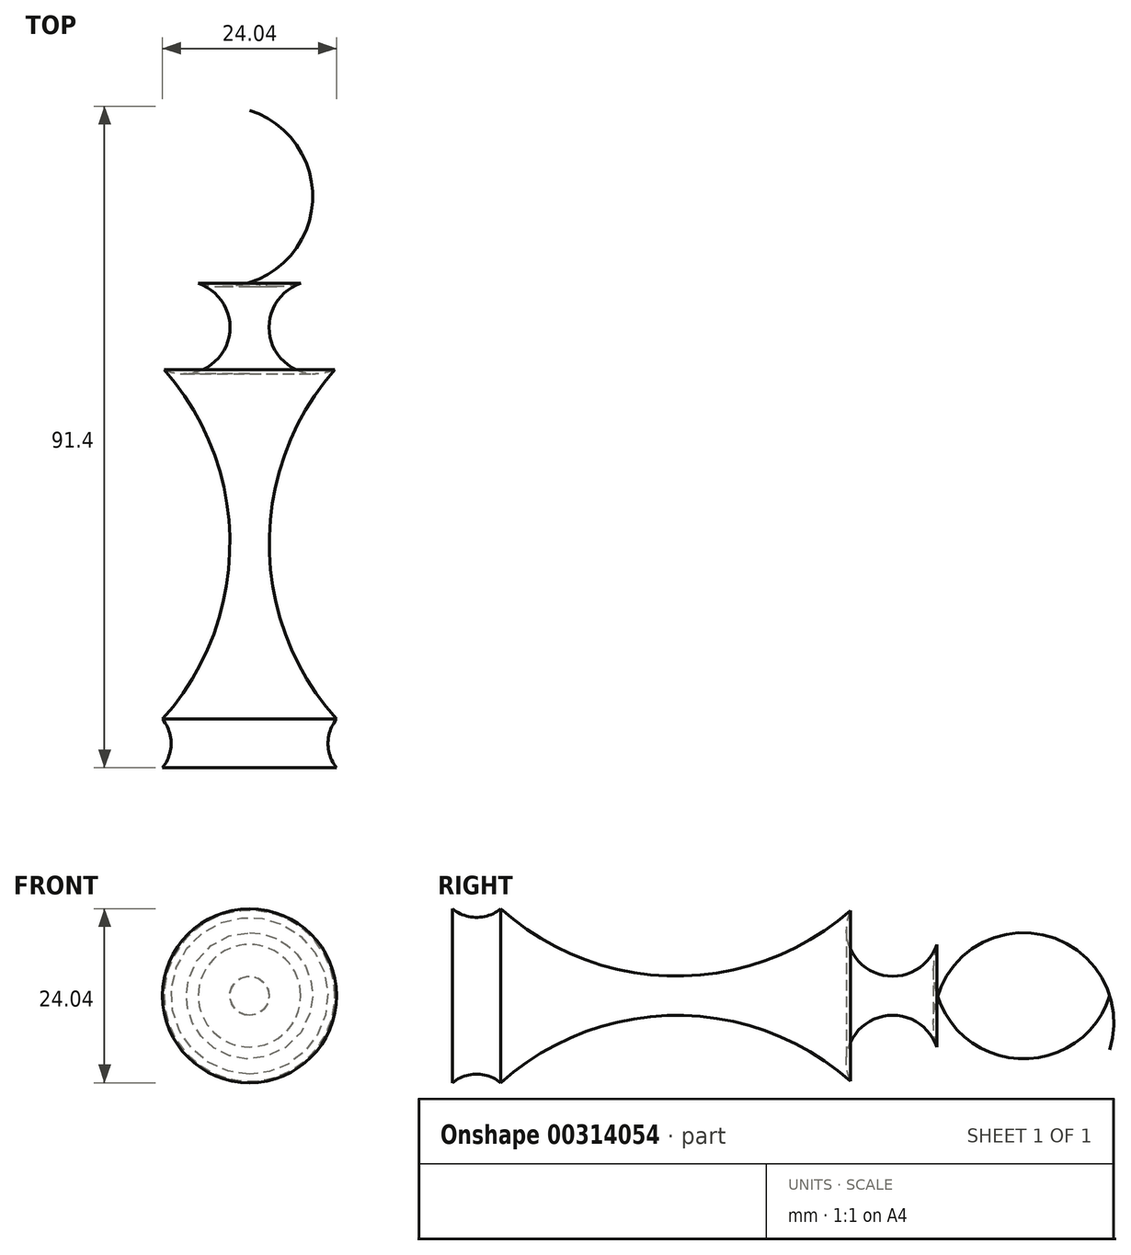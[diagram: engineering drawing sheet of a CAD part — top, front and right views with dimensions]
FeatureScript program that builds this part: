
annotation { "Feature Type Name" : "Feature", "Feature Type Description" : "" }
export const myFeature = defineFeature(function(context is Context, id is Id, definition is map)
    precondition{}
    {
        {
            var Q0;
            Q0=qCreatedBy(makeId("Top.planeOp"),FACE);
            var sketch = newSketch(context, id + "F0", { "sketchPlane" : qUnion([Q0])});
            skLineSegment(sketch, "E0", {"start": v(0, 46.48) * mm, "end": v(0, -44.34) * mm});
            skLineSegment(sketch, "E1", {"start": v(0, -44.34) * mm, "end": v(0, 46.48) * mm});
            skArc(sketch, "E2", {"start": v(0, 22.7) * mm, "mid": v(16.22, 34.59) * mm, "end": v(0, 46.48) * mm});
            skArc(sketch, "E3", {"start": v(7.5, 22.7) * mm, "mid": v(3.06, 14.34) * mm, "end": v(11.78, 10.66) * mm});
            skArc(sketch, "E4", {"start": v(11.78, 10.66) * mm, "mid": v(2.72, -13.54) * mm, "end": v(12.02, -37.64) * mm});
            skLineSegment(sketch, "E5", {"start": v(0, -44.34) * mm, "end": v(12.02, -44.34) * mm});
            skLineSegment(sketch, "E6", {"start": v(12.02, -44.34) * mm, "end": v(1.38, -44.34) * mm});
            skLineSegment(sketch, "E7", {"start": v(1.38, -44.34) * mm, "end": v(12.02, -44.34) * mm});
            skArc(sketch, "E8", {"start": v(12.02, -37.64) * mm, "mid": v(10.84, -41) * mm, "end": v(12.02, -44.34) * mm});
            skSolve(sketch);
        }
        {
            var Q0;
            {var subQ0=sQuery(id+"F0.wireOp",EDGE,"E4");Q0=makeQuery(id+"F0.imprint","IMPRINT",FACE,{"disambiguationData":[TD([[makeQuery(id+"F0.imprint","IMPRINT",EDGE,{"derivedFrom":subQ0}),-1.0]])]});}
            var Q1;
            {var subQ0=sQuery(id+"F0.wireOp",EDGE,"E2");var subQ1=sQuery(id+"F0.wireOp",EDGE,"E1");var subQ2=makeQuery(id+"F0.imprint","INTERSECT",VERTEX,{"disambiguationData":[OD(0.0)],"derivedFrom":[subQ1,subQ0]});Q1=makeQuery(id+"F0.imprint","IMPRINT",FACE,{"disambiguationData":[TD([[makeQuery(id+"F0.imprint","IMPRINT",EDGE,{"disambiguationData":[TD([[subQ2,1.0]])],"derivedFrom":subQ1}),-1.0]])]});}
            var Q2;
            Q2=sQuery(id+"F0.wireOp",EDGE,"E1");
            revolve(context, id + "F1", {"entities" : qUnion([Q0, Q1]), "axis" : qUnion([Q2]), "revolveType" : RevolveType.FULL});
        }
    });
